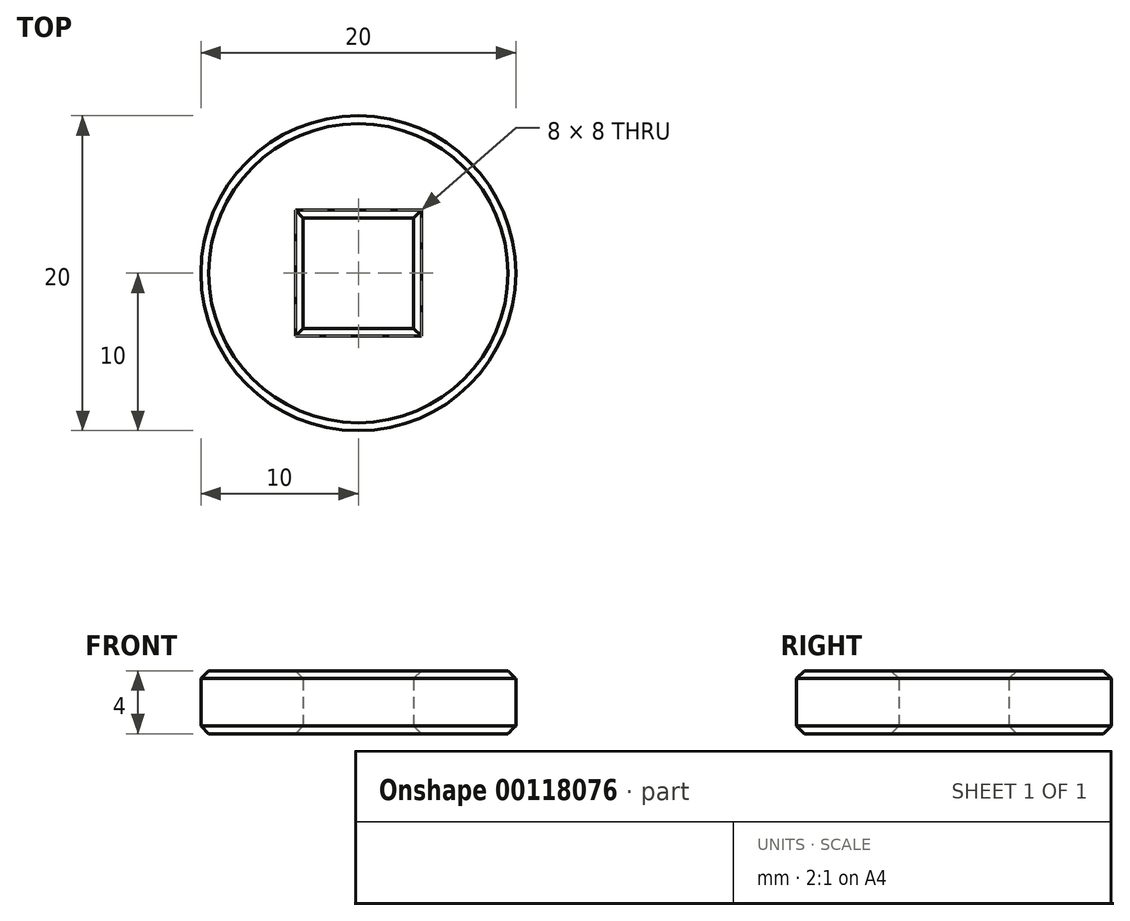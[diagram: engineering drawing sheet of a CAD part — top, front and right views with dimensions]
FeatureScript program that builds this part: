
annotation { "Feature Type Name" : "Feature", "Feature Type Description" : "" }
export const myFeature = defineFeature(function(context is Context, id is Id, definition is map)
    precondition{}
    {
        {
            var Q0;
            Q0=qCreatedBy(makeId("Top.planeOp"),FACE);
            var sketch = newSketch(context, id + "F0", { "sketchPlane" : qUnion([Q0])});
            skCircle(sketch, "E0", {"center": v(0, 0) * mm, "radius": 3.5 * mm, "construction": true});
            skCircle(sketch, "E1", {"center": v(0, 0) * mm, "radius": 10 * mm});
            skLineSegment(sketch, "E2.bottom", {"start": v(3.5, -3.5) * mm, "end": v(-3.5, -3.5) * mm});
            skLineSegment(sketch, "E2.top", {"start": v(3.5, 3.5) * mm, "end": v(-3.5, 3.5) * mm});
            skLineSegment(sketch, "E2.left", {"start": v(3.5, -3.5) * mm, "end": v(3.5, 3.5) * mm});
            skLineSegment(sketch, "E2.right", {"start": v(-3.5, -3.5) * mm, "end": v(-3.5, 3.5) * mm});
            skSolve(sketch);
        }
        {
            var Q0;
            Q0=makeQuery(id+"F0.imprint","IMPRINT",FACE,{"disambiguationData":[TD([[makeQuery(id+"F0.imprint","IMPRINT",EDGE,{"derivedFrom":sQuery(id+"F0.wireOp",EDGE,"E1")}),1.0]])]});
            extrude(context, id + "F1", {"entities" : qUnion([Q0]), "depth" : 4 * mm});
        }
        {
            var Q0;
            Q0=makeQuery(id+"F1.opExtrude","CAP_EDGE",EDGE,{"disambiguationData":[OSD([sQuery(id+"F0.wireOp",EDGE,"E1")])],"isStart":false});
            var Q1;
            Q1=makeQuery(id+"F1.opExtrude","CAP_EDGE",EDGE,{"disambiguationData":[OSD([sQuery(id+"F0.wireOp",EDGE,"E1")])],"isStart":true});
            var Q2;
            Q2=makeQuery(id+"F1.opExtrude","CAP_EDGE",EDGE,{"disambiguationData":[OSD([sQuery(id+"F0.wireOp",EDGE,"E0")])],"isStart":true});
            var Q3;
            Q3=makeQuery(id+"F1.opExtrude","CAP_EDGE",EDGE,{"disambiguationData":[OSD([sQuery(id+"F0.wireOp",EDGE,"E0")])],"isStart":false});
            chamfer(context, id + "F2", {"entities" : qUnion([Q0, Q1, Q2, Q3]), "width" : 0.5 * mm, "tangentPropagation" : true});
        }
        {
            var Q0;
            Q0=makeQuery(id+"F1.opExtrude","CAP_EDGE",EDGE,{"disambiguationData":[OSD([sQuery(id+"F0.wireOp",EDGE,"E2.top")])],"isStart":false});
            var Q1;
            Q1=makeQuery(id+"F1.opExtrude","CAP_EDGE",EDGE,{"disambiguationData":[OSD([sQuery(id+"F0.wireOp",EDGE,"E2.left")])],"isStart":false});
            var Q2;
            Q2=makeQuery(id+"F1.opExtrude","CAP_EDGE",EDGE,{"disambiguationData":[OSD([sQuery(id+"F0.wireOp",EDGE,"E2.bottom")])],"isStart":false});
            var Q3;
            Q3=makeQuery(id+"F1.opExtrude","CAP_EDGE",EDGE,{"disambiguationData":[OSD([sQuery(id+"F0.wireOp",EDGE,"E2.right")])],"isStart":false});
            var Q4;
            Q4=makeQuery(id+"F1.opExtrude","CAP_EDGE",EDGE,{"disambiguationData":[OSD([sQuery(id+"F0.wireOp",EDGE,"E2.bottom")])],"isStart":true});
            var Q5;
            Q5=makeQuery(id+"F1.opExtrude","CAP_EDGE",EDGE,{"disambiguationData":[OSD([sQuery(id+"F0.wireOp",EDGE,"E2.right")])],"isStart":true});
            var Q6;
            Q6=makeQuery(id+"F1.opExtrude","CAP_EDGE",EDGE,{"disambiguationData":[OSD([sQuery(id+"F0.wireOp",EDGE,"E2.top")])],"isStart":true});
            var Q7;
            Q7=makeQuery(id+"F1.opExtrude","CAP_EDGE",EDGE,{"disambiguationData":[OSD([sQuery(id+"F0.wireOp",EDGE,"E2.left")])],"isStart":true});
            chamfer(context, id + "F3", {"entities" : qUnion([Q0, Q1, Q2, Q3, Q4, Q5, Q6, Q7]), "width" : 0.5 * mm, "tangentPropagation" : true});
        }
    });
